# Revit family: Levelers_Kelley_EOD
name_source: partatom
category: Generic Models
units: mm (PartAtom-declared; Revit-internal decimal feet)

## family parameters
Can host rebar = No
Cut with Voids When Loaded = No
Host = Face
Maintain Annotation Orientation = No
Part Type = Normal
Room Calculation Point = No
Round Connector Dimension = Use Diameter
Shared = No

## types (8) — shared parameters
BumperHeight = 0' - 10"
Capacity = 20/30k
Default Elevation = 4' - 0"
Description = Edge Of Dock Leveler
LipLength = 1' - 3"
Manufacturer = Entrematic
Model = EOD
URL = https://www.entrematic.us

## per-type parameters (varying)
| type | DeckWidth | EmbedWidth | LipExtention |
| 72 | 6' - 0" | 7' - 0" | 0' - 0" |
| 66 PO Package | 5' - 6" | 6' - 6" | 0' - 2" |
| 72 PO Package | 6' - 0" | 7' - 0" | 0' - 2" |
| 78 | 6' - 6" | 7' - 6" | 0' - 0" |
| 78 PO Package | 6' - 6" | 7' - 6" | 0' - 2" |
| 84 | 7' - 0" | 8' - 0" | 0' - 0" |
| 84 PO Package | 7' - 0" | 8' - 0" | 0' - 2" |
| 66 | 5' - 6" | 6' - 6" | 0' - 0" |

## geometry (parser evidence)
native form markers: Sweep x3
no freeform markers — native parametric forms only
